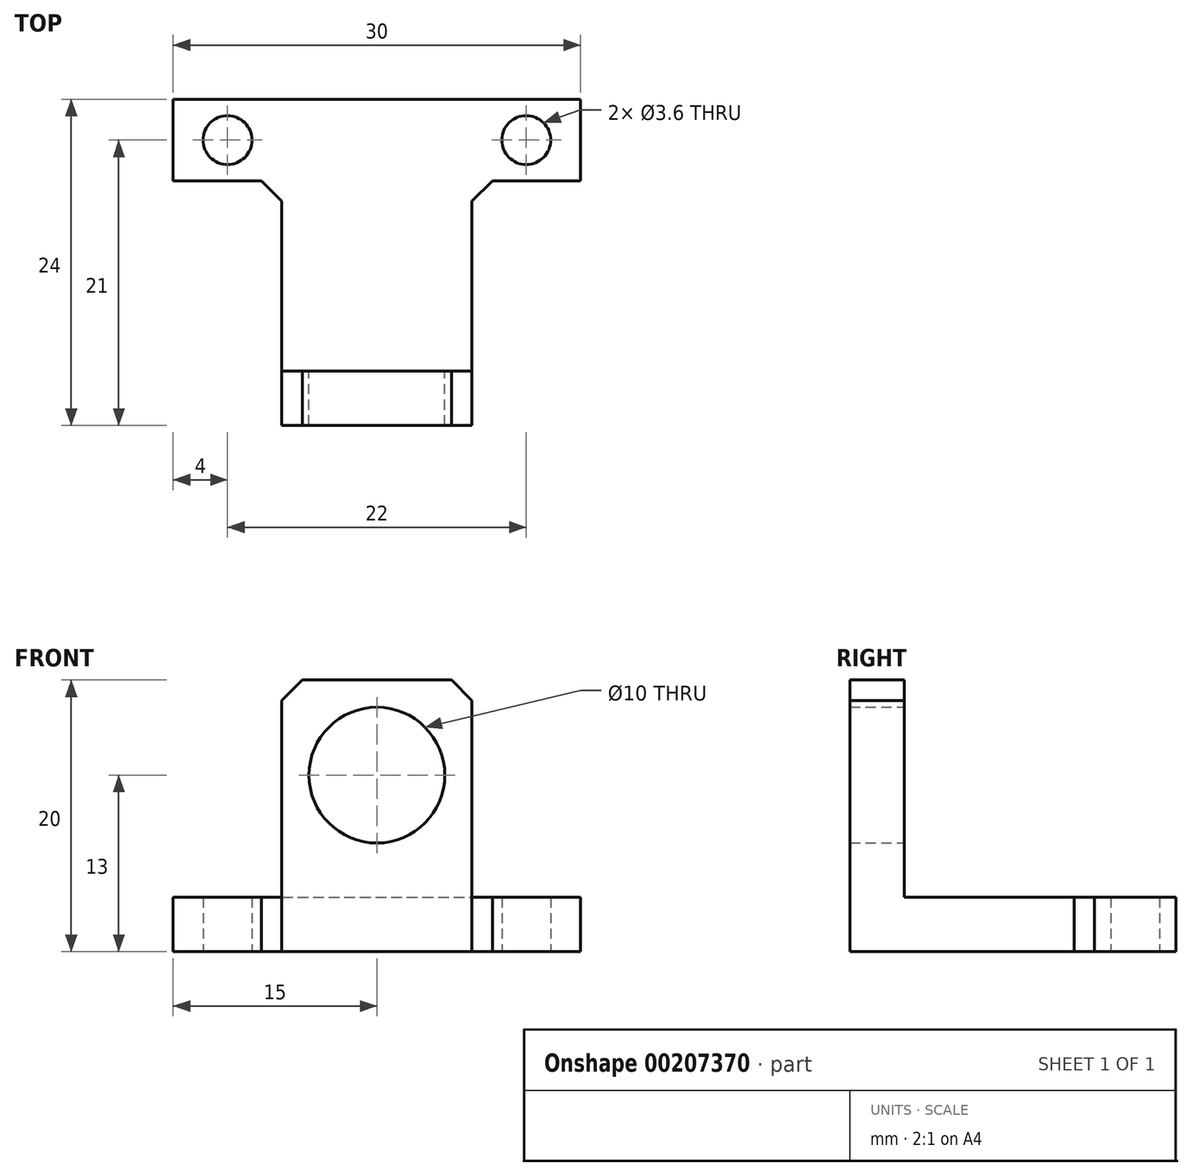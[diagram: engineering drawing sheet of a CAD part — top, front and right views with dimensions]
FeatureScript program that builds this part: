
annotation { "Feature Type Name" : "Feature", "Feature Type Description" : "" }
export const myFeature = defineFeature(function(context is Context, id is Id, definition is map)
    precondition{}
    {
        {
            var Q0;
            Q0=qCreatedBy(makeId("Top.planeOp"),FACE);
            var sketch = newSketch(context, id + "F0", { "sketchPlane" : qUnion([Q0])});
            skLineSegment(sketch, "E0.bottom", {"start": v(-30, 6) * mm, "end": v(0, 6) * mm});
            skLineSegment(sketch, "E0.top", {"start": v(-30, 0) * mm, "end": v(0, 0) * mm});
            skLineSegment(sketch, "E0.left", {"start": v(-30, 6) * mm, "end": v(-30, 0) * mm});
            skLineSegment(sketch, "E0.right", {"start": v(0, 6) * mm, "end": v(0, 0) * mm});
            skCircle(sketch, "E1", {"center": v(-26, 3) * mm, "radius": 1.8 * mm});
            skPoint(sketch, "E1.centerSnap0", {"position": v(-30, 3) * mm});
            skCircle(sketch, "E2", {"center": v(-4, 3) * mm, "radius": 1.8 * mm});
            skPoint(sketch, "E2.centerSnap0", {"position": v(0, 3) * mm});
            skLineSegment(sketch, "E3", {"start": v(-26, 3) * mm, "end": v(-4, 3) * mm, "construction": true});
            skPoint(sketch, "E4", {"position": v(-15, 6) * mm});
            skPoint(sketch, "E5", {"position": v(-15, 3) * mm});
            skLineSegment(sketch, "E6", {"start": v(-22, 0) * mm, "end": v(-22, -18) * mm});
            skLineSegment(sketch, "E7", {"start": v(-22, -18) * mm, "end": v(-8, -18) * mm});
            skLineSegment(sketch, "E8", {"start": v(-8, -18) * mm, "end": v(-8, 0) * mm});
            skPoint(sketch, "E9", {"position": v(-15, -18) * mm});
            skLineSegment(sketch, "E10", {"start": v(-22, -14) * mm, "end": v(-8, -14) * mm});
            skSolve(sketch);
        }
        {
            var Q0;
            Q0=makeQuery(id+"F0.imprint","IMPRINT",FACE,{"disambiguationData":[TD([[makeQuery(id+"F0.imprint","IMPRINT",EDGE,{"derivedFrom":sQuery(id+"F0.wireOp",EDGE,"E0.bottom")}),-1.0]])]});
            var Q1;
            {var subQ5=sQuery(id+"F0.wireOp",EDGE,"E10");Q1=makeQuery(id+"F0.imprint","IMPRINT",FACE,{"disambiguationData":[TD([[makeQuery(id+"F0.imprint","IMPRINT",EDGE,{"derivedFrom":subQ5}),1.0]])]});}
            extrude(context, id + "F1", {"entities" : qUnion([Q0, Q1]), "depth" : 4 * mm});
        }
        {
            var Q0;
            {var subQ0=sQuery(id+"F0.wireOp",EDGE,"E7");Q0=makeQuery(id+"F0.imprint","IMPRINT",FACE,{"disambiguationData":[TD([[makeQuery(id+"F0.imprint","IMPRINT",EDGE,{"derivedFrom":subQ0}),1.0]])]});}
            extrude(context, id + "F2", {"entities" : qUnion([Q0]), "operationType" : NewBodyOperationType.ADD, "depth" : 20 * mm});
        }
        {
            var Q0;
            Q0=makeQuery(id+"F2.opExtrude","SWEPT_FACE",FACE,{"disambiguationData":[OSD([sQuery(id+"F0.wireOp",EDGE,"E10")])]});
            var sketch = newSketch(context, id + "F3", { "sketchPlane" : qUnion([Q0])});
            skCircle(sketch, "E11", {"center": v(15, 13) * mm, "radius": 5 * mm});
            skSolve(sketch);
        }
        {
            var Q0;
            Q0=makeQuery(id+"F3.imprint","IMPRINT",FACE,{"disambiguationData":[TD([[makeQuery(id+"F3.imprint","IMPRINT",EDGE,{"derivedFrom":sQuery(id+"F3.wireOp",EDGE,"E11")}),1.0]])]});
            extrude(context, id + "F4", {"entities" : qUnion([Q0]), "operationType" : NewBodyOperationType.REMOVE, "endBound" : BoundingType.UP_TO_NEXT, "oppositeDirection" : true, "depth" : 25 * mm});
        }
        {
            var Q0;
            Q0=makeQuery(id+"F1.opExtrude","CAP_EDGE",EDGE,{"disambiguationData":[OSD([sQuery(id+"F0.wireOp",EDGE,"E10")])],"isStart":false});
            var Q1;
            Q1=makeQuery(id+"F2.opExtrude","CAP_EDGE",EDGE,{"disambiguationData":[OSD([sQuery(id+"F0.wireOp",EDGE,"E6")])],"isStart":false});
            var Q2;
            Q2=makeQuery(id+"F2.opExtrude","CAP_EDGE",EDGE,{"disambiguationData":[OSD([sQuery(id+"F0.wireOp",EDGE,"E8")])],"isStart":false});
            var Q3;
            Q3=makeQuery(id+"F1.opExtrude","SWEPT_EDGE",EDGE,{"disambiguationData":[OSD([sQuery(id+"F0.wireOp",EDGE,"E0.top"),sQuery(id+"F0.wireOp",EDGE,"E6")])]});
            var Q4;
            Q4=makeQuery(id+"F1.opExtrude","SWEPT_EDGE",EDGE,{"disambiguationData":[OSD([sQuery(id+"F0.wireOp",EDGE,"E0.top"),sQuery(id+"F0.wireOp",EDGE,"E8")])]});
            chamfer(context, id + "F5", {"entities" : qUnion([Q0, Q1, Q2, Q3, Q4]), "width" : 1.5 * mm, "tangentPropagation" : true});
        }
    });
